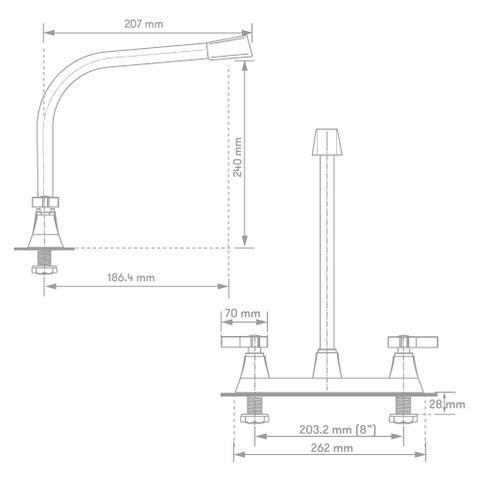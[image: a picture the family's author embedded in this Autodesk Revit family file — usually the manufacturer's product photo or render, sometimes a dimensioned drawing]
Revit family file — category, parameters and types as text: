
# Revit family: 01-3628-11 MEZCLADOR LAVAPLATOS 8 FIRENZE PALA
name_source: partatom
category: Aparatos sanitarios
revit_build: Autodesk Revit 2018 (Build: 20170223_1515(x64)
units: mm (PartAtom-declared; Revit-internal decimal feet)

## family parameters
Anfitrión = Cara
Compartido = No
Corte con vacíos al cargar = No
Cota de conector redondo = Diámetro de uso
Número OmniClass = 23.31.11.00
Punto de cálculo de habitación = No
Tipo de pieza = Normal

## types (1)
- 01-3628-11
    Alto brazo = 240 mm  [stored 0.787402 ft]
    Ancho brazo = 207 mm
    Ancho entre manijas = 203.2 mm
    Ancho manija = 65 mm  [stored 0.213255 ft]
    Conexión AC = Sí
    Conexión AF = Sí
    Conexión de residuos = No
    Conexión de ventilación = No
    Descripción = Bimando
    Elevación por defecto = 0 mm  [stored 0 ft]
    Fabricante = Gricol
    Imagen de tipo = <Ninguno>
    Link Ficha Tecnica = http://infotecnica.gricol.com
    Metal Laton Cromado = Metal Laton Cromado
    Metal Zamak Cromado = Metal Zamak Cromado
    Modelo = 01-3628-11
    Plástico - ABS Cromado = Plastico ABS Cromado
    Product Name = MEZCLADOR LAVAPLATOS 8 FIRENZE PALA
    URL = https://www.gricol.com

note: [stored X ft] marks values corroborated as IEEE doubles in the binary element streams (Revit-internal decimal feet)

## geometry (parser evidence)
native form markers: Blend x2, Sweep x6
no freeform markers — native parametric forms only
